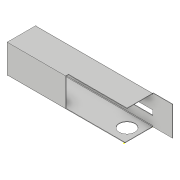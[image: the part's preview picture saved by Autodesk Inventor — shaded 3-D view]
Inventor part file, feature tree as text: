
AUTODESK INVENTOR PART (.ipt)
format: ipt  version: 2019 (Build 230136000, 136)  size: 173,056 bytes
history: native  units: mm
features: sheet_metal_op x12, sketch x11, other x5, extrude x4
ambient origin geometry x8: Origin, YZ Plane, XZ Plane, XY Plane, X Axis, Y Axis, Z Axis, Center Point
bodies: Solid1 (feature_tree)
feature tree (32):
  sheet_metal_op  "Face1"
  extrude  "Extrusion1"  Depth=30.0mm
  sheet_metal_op  "Flange1"
  sheet_metal_op  "Flange2"
  sheet_metal_op  "Flange3"
  sketch  "Sketch6"  dims[d10=1.0mm]
  extrude  "Extrusion2"  Depth=10.0mm
  extrude  "Extrusion3"  Depth=5.0mm
  extrude  "Extrusion4"  Depth=0.5mm
  sketch  "Sketch10"  dims[d16=0.5mm]
  sheet_metal_op  "Face2"
  sketch  "Sketch1"  dims[d0=120.0mm d1=30.0mm]
  other  "Plate1"
  sketch  "Sketch2"  dims[d2=0.5mm d3=10.0mm]
  sketch  "Sketch3"  dims[d4=25.0mm d5=5.0mm]
  other  "Plate2"
  sheet_metal_op  "Bend1"
  sheet_metal_op  "Corner1"
  sketch  "Sketch4"  dims[d6=3.0mm d7=0.0mm d8=0.5mm]
  other  "Plate3"
  sheet_metal_op  "Bend2"
  sheet_metal_op  "Corner2"
  sketch  "Sketch5"  dims[d9=0.25mm]
  other  "Plate4"
  sheet_metal_op  "Bend3"
  sheet_metal_op  "Corner3"
  sketch  "Sketch7"  dims[d11=0.5mm]
  sketch  "Sketch8"  dims[d12=30.0mm d13=90.0deg d14=0.5mm]
  sketch  "Sketch9"  dims[d15=2.0mm]
  sketch  "Sketch11"  dims[d17=0.5mm d18=0.5mm d19=0.25mm d20=1.0mm d21=0.5mm d22=30.0mm d23=90.0deg d24=0.5mm d25=2.0mm d26=0.5mm d27=0.5mm d28=0.5mm d29=0.25mm d30=1.0mm d31=0.5mm d32=30.0mm d33=90.0deg d34=0.5mm d35=2.0mm d36=0.5mm d37=0.5mm d38=60.0mm d39=30.0mm d40=3.0mm d41=0.0mm d42=3.0mm d43=0.0mm d44=16.0mm d45=3.0mm d46=0.0mm d47=20.0mm d48=0.5mm d49=0.5mm d50=0.25mm d51=1.0mm d52=0.5mm]
  other  "Plate5"
  sheet_metal_op  "Bend4"
